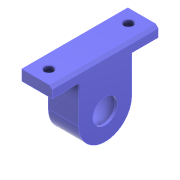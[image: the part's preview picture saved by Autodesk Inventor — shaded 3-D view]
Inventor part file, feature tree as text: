
AUTODESK INVENTOR PART (.ipt)
format: ipt  version: 2022 (Build 260153000, 153)  size: 173,568 bytes
history: native  units: mm
features: sketch x5, projected_geometry x4, extrude x3, hole x2, chamfer x2, thicken_offset x1
ambient origin geometry x8: Origin, YZ Plane, XZ Plane, XY Plane, X Axis, Y Axis, Z Axis, Center Point
bodies: Solid1 (feature_tree)
feature tree (17):
  extrude  "Extrusion1"  Depth=14.0mm
  extrude  "Extrusion2"  Depth=4.0mm TaperAngle=0.0deg
  hole  "Hole1"  [1 undecoded]
  hole  "Hole3"  [1 undecoded]
  thicken_offset  "Thicken1"
  extrude  "Extrusion3"  Depth=5.0mm
  chamfer  "Chamfer2"  Distance=0.15mm
  chamfer  "Chamfer3"  Distance=2.0mm
  sketch  "Sketch1"  dims[d2=20.0mm d1=14.0mm]
  sketch  "Sketch2"  dims[d3=0.0mm d5=4.0mm d6=0.0mm]
  sketch  "Sketch3"  dims[d7=3.4mm d8=6.0mm d9=6.0mm d10=2.0mm d11=90.0deg d12=8.0mm d13=20.594885mm d21=13.0mm]
  sketch  "Sketch5"  dims[d22=6.0mm d23=4.0mm d24=2.0mm d25=90.0deg d26=8.0mm d27=20.594885mm d28=40.0mm]
  sketch  "Sketch6"  dims[d30=5.0mm d31=5.0mm d32=0.15mm d33=0.15mm d37=2.0mm d38=1.0mm d39=0.0mm d40=0.5mm d41=2.0mm d42=45.0deg d43=1.0mm d44=2.0mm d45=45.0deg d46=0.5mm d47=0.872665mm d48=0.5mm d49=0.872665mm]
  projected_geometry  "Project Cut Edges1"
  projected_geometry  "Project Cut Edges2"
  projected_geometry  "Project Cut Edges3"
  projected_geometry  "Project Cut Edges4"
note: 2 required parameter values undecoded (feature->parameter linkage not recoverable at this tier; creation-order binding heuristic only, values carry confidence <= 0.55)
